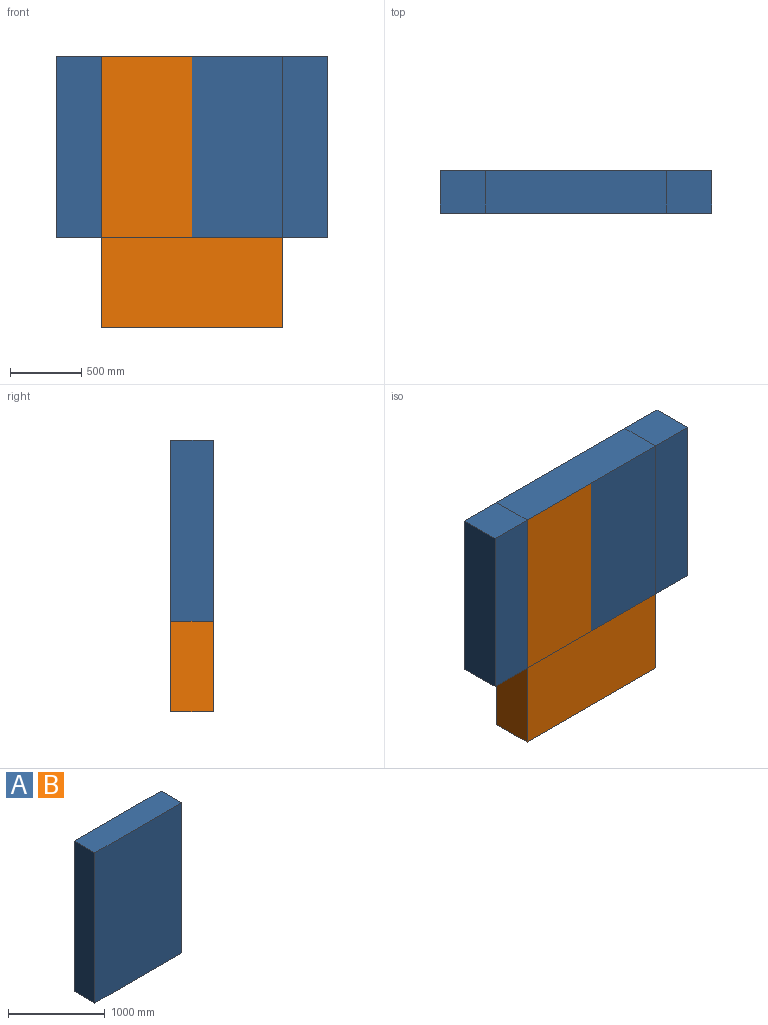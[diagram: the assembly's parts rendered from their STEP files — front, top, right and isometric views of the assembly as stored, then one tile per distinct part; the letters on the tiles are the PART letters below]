
ASSEMBLY  parts=2 mates=1
PART A: 6 faces, bbox 1270x300x1905 mm
  f0: plane 1905x300mm, normal (-1,0,0), area 571500mm2, adj f1,f3,f4,f5
  f1: plane 1270x300mm, normal (0,0,-1), area 381000mm2, adj f0,f2,f4,f5
  f2: plane 1905x300mm, normal (1,0,0), area 571500mm2, adj f1,f3,f4,f5
  f3: plane 1270x300mm, normal (0,0,1), area 381000mm2, adj f0,f2,f4,f5
  f4: plane 1905x1270mm, normal (0,-1,0), area 2419350mm2, adj f0,f1,f2,f3
  f5: plane 1905x1270mm, normal (0,1,0), area 2419350mm2, adj f0,f1,f2,f3
PART B: same geometry as A
PLACE A rot(axis=(0,-1,0),90deg) t=(368.72,223.01,297.58)mm
PLACE B t=(-1218.78,223.01,-337.42)mm
MATE revolute A.f2 <-> B.f3  axis (0,0,1) through (-583.78,73.01,1567.58)mm
